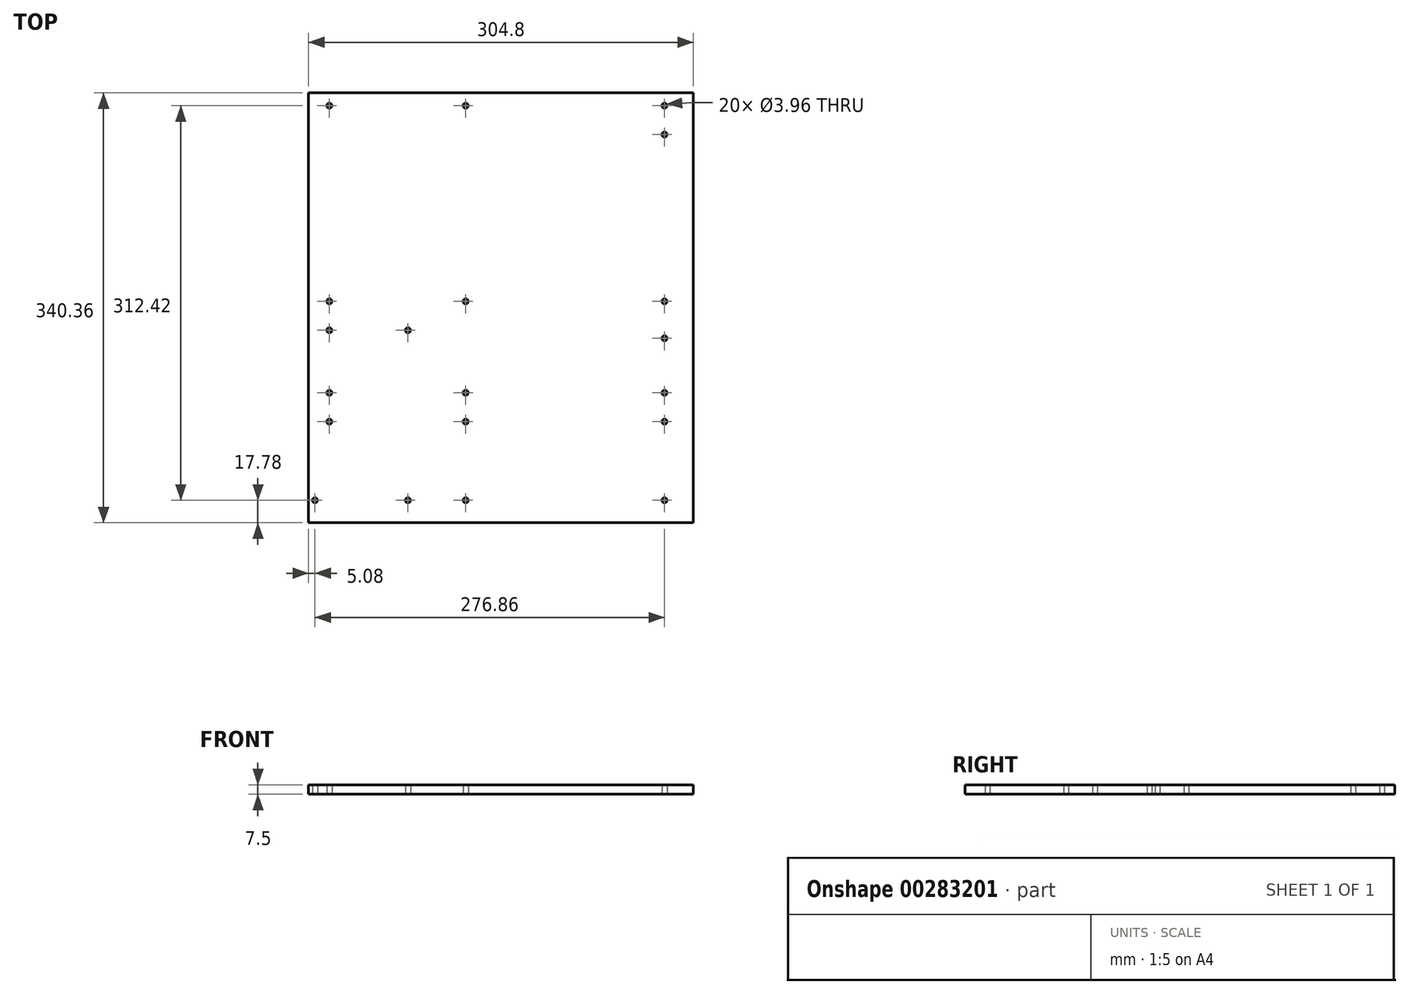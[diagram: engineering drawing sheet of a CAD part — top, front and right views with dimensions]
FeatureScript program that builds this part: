
annotation { "Feature Type Name" : "Feature", "Feature Type Description" : "" }
export const myFeature = defineFeature(function(context is Context, id is Id, definition is map)
    precondition{}
    {
        {
            var Q0;
            Q0=qCreatedBy(makeId("Top.planeOp"),FACE);
            var sketch = newSketch(context, id + "F0", { "sketchPlane" : qUnion([Q0])});
            skLineSegment(sketch, "E0.bottom", {"start": v(152.4, -170.18) * mm, "end": v(-152.4, -170.18) * mm});
            skLineSegment(sketch, "E0.top", {"start": v(152.4, 170.18) * mm, "end": v(-152.4, 170.18) * mm});
            skLineSegment(sketch, "E0.left", {"start": v(152.4, -170.18) * mm, "end": v(152.4, 170.18) * mm});
            skLineSegment(sketch, "E0.right", {"start": v(-152.4, -170.18) * mm, "end": v(-152.4, 170.18) * mm});
            skPoint(sketch, "E0.middle", {"position": v(0, 0) * mm});
            skLineSegment(sketch, "E1", {"start": v(-152.4, 170.18) * mm, "end": v(-135.9, 170.18) * mm, "construction": true});
            skLineSegment(sketch, "E2", {"start": v(-135.9, 170.18) * mm, "end": v(-135.9, 160.02) * mm, "construction": true});
            skLineSegment(sketch, "E3", {"start": v(-135.9, 160.02) * mm, "end": v(-135.9, 5.08) * mm, "construction": true});
            skLineSegment(sketch, "E4", {"start": v(-135.9, 5.08) * mm, "end": v(-135.9, -17.78) * mm, "construction": true});
            skLineSegment(sketch, "E5", {"start": v(-135.9, -17.78) * mm, "end": v(-135.9, -67.31) * mm, "construction": true});
            skLineSegment(sketch, "E6", {"start": v(-135.9, -67.31) * mm, "end": v(-135.9, -90.17) * mm, "construction": true});
            skLineSegment(sketch, "E7", {"start": v(-147.32, -152.4) * mm, "end": v(-152.4, -152.4) * mm, "construction": true});
            skLineSegment(sketch, "E8", {"start": v(-147.32, -152.4) * mm, "end": v(-73.66, -152.4) * mm, "construction": true});
            skLineSegment(sketch, "E9", {"start": v(-73.66, -152.4) * mm, "end": v(-27.94, -152.4) * mm, "construction": true});
            skLineSegment(sketch, "E10", {"start": v(-27.94, -152.4) * mm, "end": v(129.54, -152.4) * mm, "construction": true});
            skLineSegment(sketch, "E11", {"start": v(-135.9, 160.02) * mm, "end": v(-27.94, 160.02) * mm, "construction": true});
            skLineSegment(sketch, "E12", {"start": v(-27.94, 160.02) * mm, "end": v(129.54, 160.02) * mm, "construction": true});
            skLineSegment(sketch, "E13", {"start": v(129.54, 160.02) * mm, "end": v(129.54, 137.16) * mm, "construction": true});
            skLineSegment(sketch, "E14", {"start": v(-135.9, 5.08) * mm, "end": v(-27.94, 5.08) * mm, "construction": true});
            skLineSegment(sketch, "E15", {"start": v(-27.94, 5.08) * mm, "end": v(129.54, 5.08) * mm, "construction": true});
            skLineSegment(sketch, "E16", {"start": v(129.54, 5.08) * mm, "end": v(129.54, -24.13) * mm, "construction": true});
            skLineSegment(sketch, "E17", {"start": v(-135.9, -17.78) * mm, "end": v(-73.66, -17.78) * mm, "construction": true});
            skLineSegment(sketch, "E18", {"start": v(-135.9, -67.31) * mm, "end": v(-27.94, -67.31) * mm, "construction": true});
            skLineSegment(sketch, "E19", {"start": v(-27.94, -67.31) * mm, "end": v(129.54, -67.3) * mm, "construction": true});
            skLineSegment(sketch, "E20", {"start": v(-135.9, -90.17) * mm, "end": v(-27.94, -90.17) * mm, "construction": true});
            skLineSegment(sketch, "E21", {"start": v(-27.94, -90.17) * mm, "end": v(129.54, -90.17) * mm, "construction": true});
            skLineSegment(sketch, "E22", {"start": v(-27.94, 160.02) * mm, "end": v(-27.94, 5.08) * mm, "construction": true});
            skLineSegment(sketch, "E23", {"start": v(-27.94, -67.31) * mm, "end": v(-27.94, -90.17) * mm, "construction": true});
            skLineSegment(sketch, "E24", {"start": v(-27.94, 5.08) * mm, "end": v(-27.94, -67.31) * mm, "construction": true});
            skLineSegment(sketch, "E25", {"start": v(129.54, 137.16) * mm, "end": v(129.54, 5.08) * mm, "construction": true});
            skLineSegment(sketch, "E26", {"start": v(129.54, -24.13) * mm, "end": v(129.54, -67.3) * mm, "construction": true});
            skLineSegment(sketch, "E27", {"start": v(129.54, -90.17) * mm, "end": v(129.54, -67.3) * mm, "construction": true});
            skLineSegment(sketch, "E28", {"start": v(-27.94, -90.17) * mm, "end": v(-27.94, -152.4) * mm, "construction": true});
            skLineSegment(sketch, "E29", {"start": v(129.54, -90.17) * mm, "end": v(129.54, -152.4) * mm, "construction": true});
            skLineSegment(sketch, "E30", {"start": v(-73.66, -17.78) * mm, "end": v(-73.66, -152.4) * mm, "construction": true});
            skCircle(sketch, "E31", {"center": v(-135.9, 160.02) * mm, "radius": 1.98 * mm});
            skCircle(sketch, "E32", {"center": v(-27.94, 160.02) * mm, "radius": 1.98 * mm});
            skCircle(sketch, "E33", {"center": v(-135.9, 5.08) * mm, "radius": 1.98 * mm});
            skCircle(sketch, "E34", {"center": v(-135.9, -17.78) * mm, "radius": 1.98 * mm});
            skCircle(sketch, "E35", {"center": v(-135.9, -67.31) * mm, "radius": 1.98 * mm});
            skCircle(sketch, "E36", {"center": v(-135.9, -90.17) * mm, "radius": 1.98 * mm});
            skCircle(sketch, "E37", {"center": v(-147.32, -152.4) * mm, "radius": 1.98 * mm});
            skCircle(sketch, "E38", {"center": v(-73.66, -152.4) * mm, "radius": 1.98 * mm});
            skCircle(sketch, "E39", {"center": v(-27.94, -152.4) * mm, "radius": 1.98 * mm});
            skCircle(sketch, "E40", {"center": v(-27.94, -90.17) * mm, "radius": 1.98 * mm});
            skCircle(sketch, "E41", {"center": v(-27.94, -67.31) * mm, "radius": 1.98 * mm});
            skCircle(sketch, "E42", {"center": v(-27.94, 5.08) * mm, "radius": 1.98 * mm});
            skCircle(sketch, "E43", {"center": v(129.54, -152.4) * mm, "radius": 1.98 * mm});
            skCircle(sketch, "E44", {"center": v(129.54, -90.17) * mm, "radius": 1.98 * mm});
            skCircle(sketch, "E45", {"center": v(129.54, -67.3) * mm, "radius": 1.98 * mm});
            skCircle(sketch, "E46", {"center": v(129.54, -24.13) * mm, "radius": 1.98 * mm});
            skCircle(sketch, "E47", {"center": v(129.54, 5.08) * mm, "radius": 1.98 * mm});
            skCircle(sketch, "E48", {"center": v(129.54, 137.16) * mm, "radius": 1.98 * mm});
            skCircle(sketch, "E49", {"center": v(129.54, 160.02) * mm, "radius": 1.98 * mm});
            skCircle(sketch, "E50", {"center": v(-73.66, -17.78) * mm, "radius": 1.98 * mm});
            skSolve(sketch);
        }
        {
            var Q0;
            Q0 = qSketchRegion(id + "F0", true);
            extrude(context, id + "F1", {"entities" : qUnion([Q0]), "endBound" : BoundingType.SYMMETRIC, "depth" : 7.5 * mm});
        }
    });
